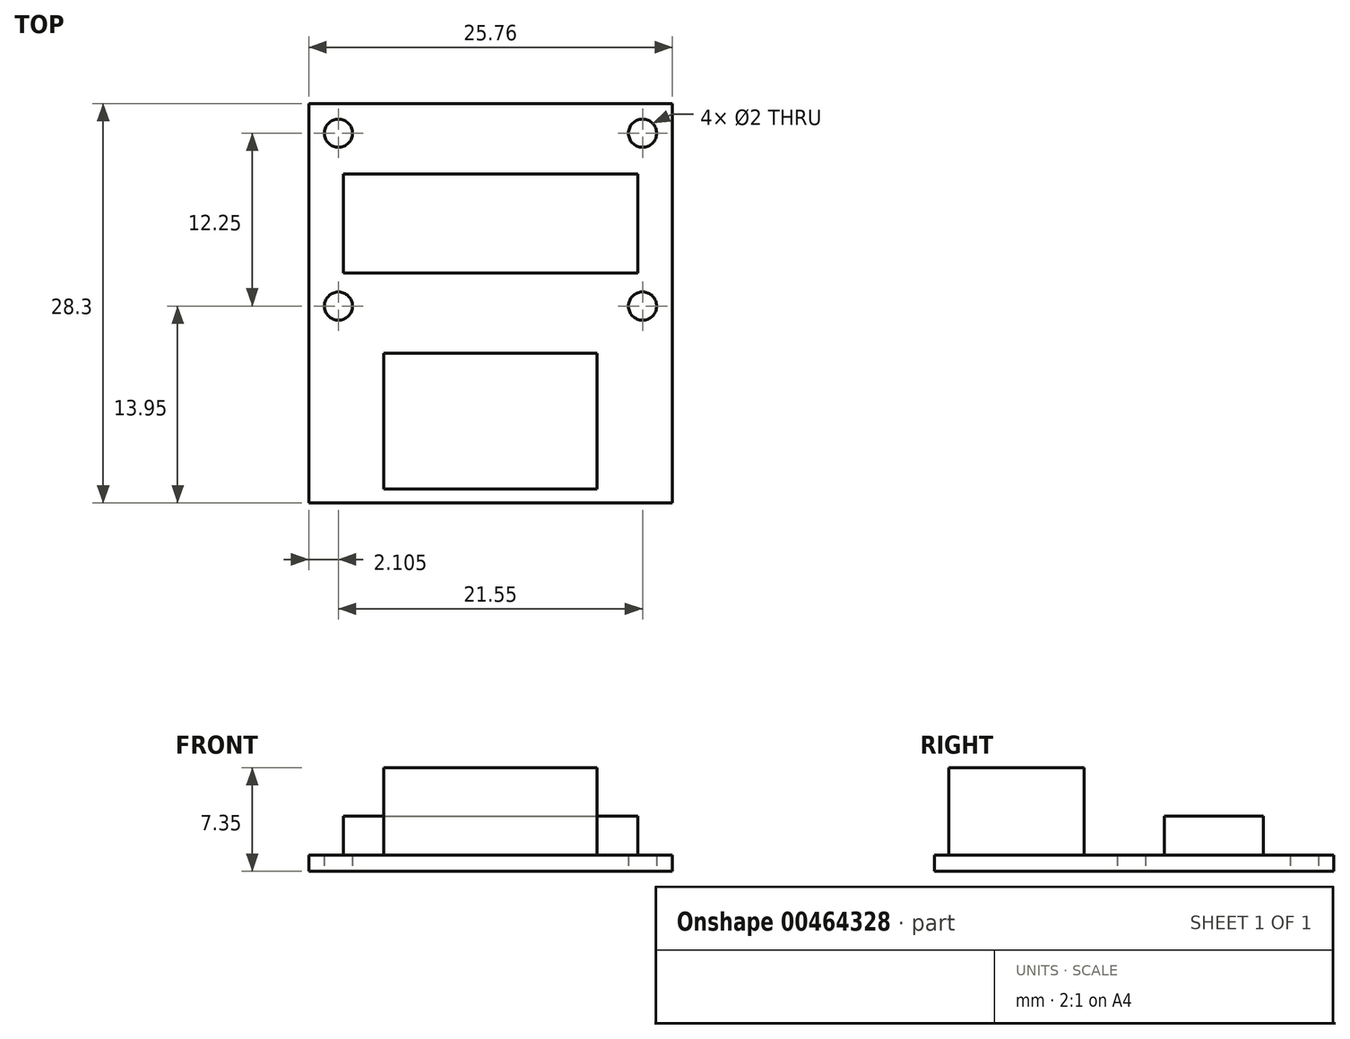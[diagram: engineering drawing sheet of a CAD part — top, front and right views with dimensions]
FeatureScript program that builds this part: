
annotation { "Feature Type Name" : "Feature", "Feature Type Description" : "" }
export const myFeature = defineFeature(function(context is Context, id is Id, definition is map)
    precondition{}
    {
        {
            var Q0;
            Q0=qCreatedBy(makeId("Top.planeOp"),FACE);
            var sketch = newSketch(context, id + "F0", { "sketchPlane" : qUnion([Q0])});
            skLineSegment(sketch, "E0.bottom", {"start": v(-12.88, 14.15) * mm, "end": v(12.88, 14.15) * mm});
            skLineSegment(sketch, "E0.top", {"start": v(-12.88, -14.15) * mm, "end": v(12.88, -14.15) * mm});
            skLineSegment(sketch, "E0.left", {"start": v(-12.88, 14.15) * mm, "end": v(-12.88, -14.15) * mm});
            skLineSegment(sketch, "E0.right", {"start": v(12.88, 14.15) * mm, "end": v(12.87, -14.15) * mm});
            skPoint(sketch, "E1", {"position": v(0, 14.15) * mm});
            skPoint(sketch, "E2", {"position": v(0, -14.15) * mm});
            skPoint(sketch, "E3", {"position": v(12.88, 0) * mm});
            skPoint(sketch, "E4", {"position": v(-12.88, 0) * mm});
            skLineSegment(sketch, "E5.bottom", {"start": v(-7.55, -3.55) * mm, "end": v(7.55, -3.55) * mm});
            skLineSegment(sketch, "E5.top", {"start": v(-7.55, -13.15) * mm, "end": v(7.55, -13.15) * mm});
            skLineSegment(sketch, "E5.left", {"start": v(-7.55, -3.55) * mm, "end": v(-7.55, -13.15) * mm});
            skLineSegment(sketch, "E5.right", {"start": v(7.55, -3.55) * mm, "end": v(7.55, -13.15) * mm});
            skPoint(sketch, "E6", {"position": v(0, -3.55) * mm});
            skPoint(sketch, "E7", {"position": v(0, -13.15) * mm});
            skLineSegment(sketch, "E8.bottom", {"start": v(-10.43, 9.15) * mm, "end": v(10.43, 9.15) * mm});
            skLineSegment(sketch, "E8.top", {"start": v(-10.43, 2.15) * mm, "end": v(10.43, 2.15) * mm});
            skLineSegment(sketch, "E8.left", {"start": v(-10.43, 9.15) * mm, "end": v(-10.43, 2.15) * mm});
            skLineSegment(sketch, "E8.right", {"start": v(10.42, 9.15) * mm, "end": v(10.42, 2.15) * mm});
            skPoint(sketch, "E9", {"position": v(0, 9.15) * mm});
            skPoint(sketch, "E10", {"position": v(0, 2.15) * mm});
            skCircle(sketch, "E11", {"center": v(-10.77, 12.05) * mm, "radius": 1 * mm});
            skCircle(sketch, "E12", {"center": v(10.78, 12.05) * mm, "radius": 1 * mm});
            skCircle(sketch, "E13", {"center": v(10.78, -0.2) * mm, "radius": 1 * mm});
            skCircle(sketch, "E14", {"center": v(-10.77, -0.2) * mm, "radius": 1 * mm});
            skSolve(sketch);
        }
        {
            var Q0;
            Q0=makeQuery(id+"F0.imprint","IMPRINT",FACE,{"disambiguationData":[TD([[makeQuery(id+"F0.imprint","IMPRINT",EDGE,{"derivedFrom":sQuery(id+"F0.wireOp",EDGE,"E0.bottom")}),-1.0]])]});
            extrude(context, id + "F1", {"entities" : qUnion([Q0]), "depth" : 1.15 * mm});
        }
        {
            var Q0;
            Q0=makeQuery(id+"F0.imprint","IMPRINT",FACE,{"disambiguationData":[TD([[makeQuery(id+"F0.imprint","IMPRINT",EDGE,{"derivedFrom":sQuery(id+"F0.wireOp",EDGE,"E8.bottom")}),-1.0]])]});
            extrude(context, id + "F2", {"entities" : qUnion([Q0]), "operationType" : NewBodyOperationType.ADD, "depth" : 3.9 * mm});
        }
        {
            var Q0;
            Q0=makeQuery(id+"F0.imprint","IMPRINT",FACE,{"disambiguationData":[TD([[makeQuery(id+"F0.imprint","IMPRINT",EDGE,{"derivedFrom":sQuery(id+"F0.wireOp",EDGE,"E5.bottom")}),-1.0]])]});
            extrude(context, id + "F3", {"entities" : qUnion([Q0]), "operationType" : NewBodyOperationType.ADD, "depth" : 7.35 * mm});
        }
    });
